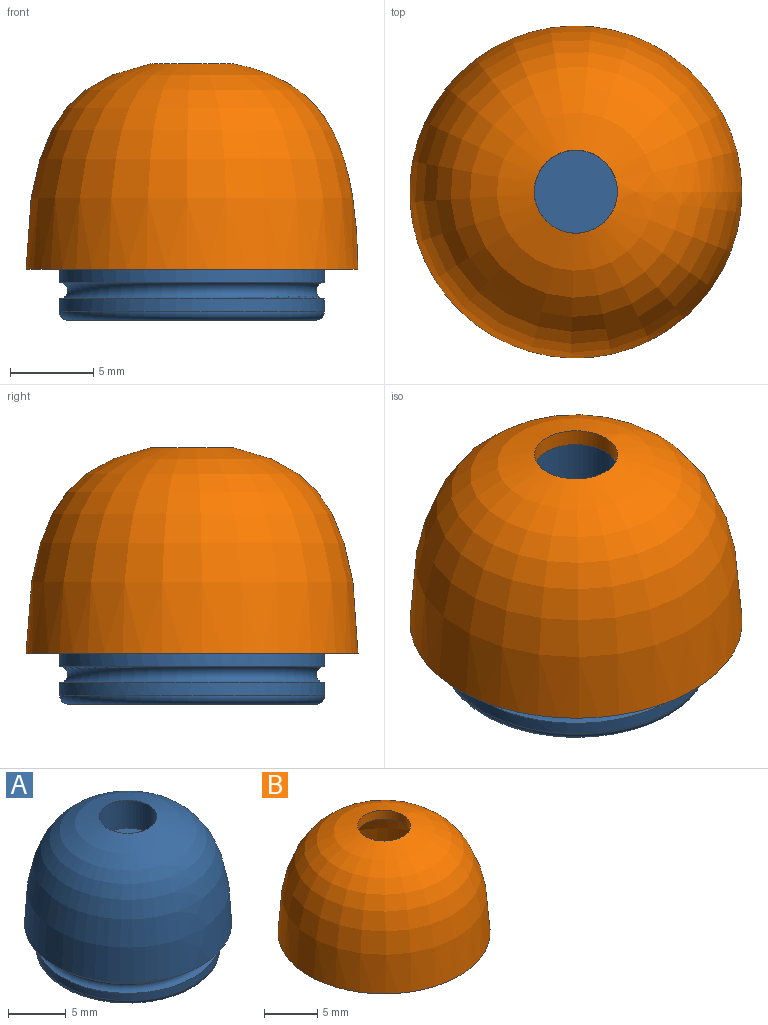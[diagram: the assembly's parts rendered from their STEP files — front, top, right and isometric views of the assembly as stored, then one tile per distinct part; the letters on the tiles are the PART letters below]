
ASSEMBLY  parts=2 mates=1
PART A: 13 faces, bbox 18x18x14.4 mm
  f0: cylinder r=7.98mm len=15.96mm, axis (0,0,1), area 38.8mm2, adj f2,f7
  f1: plane 6x6mm, normal (0,0,-1), area 28.3mm2, adj f6
  f2: torus R=7.48mm, axis (0,0,1), area 38.5mm2, adj f0,f3
  f3: plane 14.96x14.96mm, normal (0,0,-1), area 37.5mm2, adj f2,f4
  f4: revolved ~14x14mm, area 134.2mm2, adj f3,f5
  f5: revolved ~14x14mm, area 402.2mm2, adj f4,f6
  f6: cylinder r=3mm len=6mm, axis (0,0,1), area 32mm2, adj f1,f5
  f7: torus R=7.98mm, axis (0,0,-1), area 75.6mm2, adj f0,f10
  f8: revolved ~18x18mm, area 1296.3mm2, adj f9,f11
  f9: plane 18x18mm, normal (0,0,-1), area 54.4mm2, adj f8,f10
  f10: cylinder r=7.98mm len=15.96mm, axis (0,0,1), area 40.1mm2, adj f7,f9
  f11: cylinder r=2.5mm len=5mm, axis (0,0,1), area 47mm2, adj f8,f12
  f12: plane 5x5mm, normal (0,0,1), area 19.6mm2, adj f11
PART B: 4 faces, bbox 20x20x12.4 mm
  f0: revolved ~20x20mm, area 785.4mm2, adj f1,f3
  f1: plane 20x20mm, normal (0,0,-1), area 59.7mm2, adj f0,f2
  f2: revolved ~18x18mm, area 648.1mm2, adj f1,f3
  f3: cylinder r=2.5mm len=5.01mm, axis (0,0,1), area 16mm2, adj f0,f2
PLACE A rot(axis=(-1,0,0),0deg) t=(9.21,7.92,-0.32)mm
PLACE B rot(axis=(-1,0,0),0deg) t=(9.21,7.92,-0.32)mm
MATE fastened B.f3 <-> A.f0  axis (0,0,1) through (9.21,7.92,-0.32)mm
